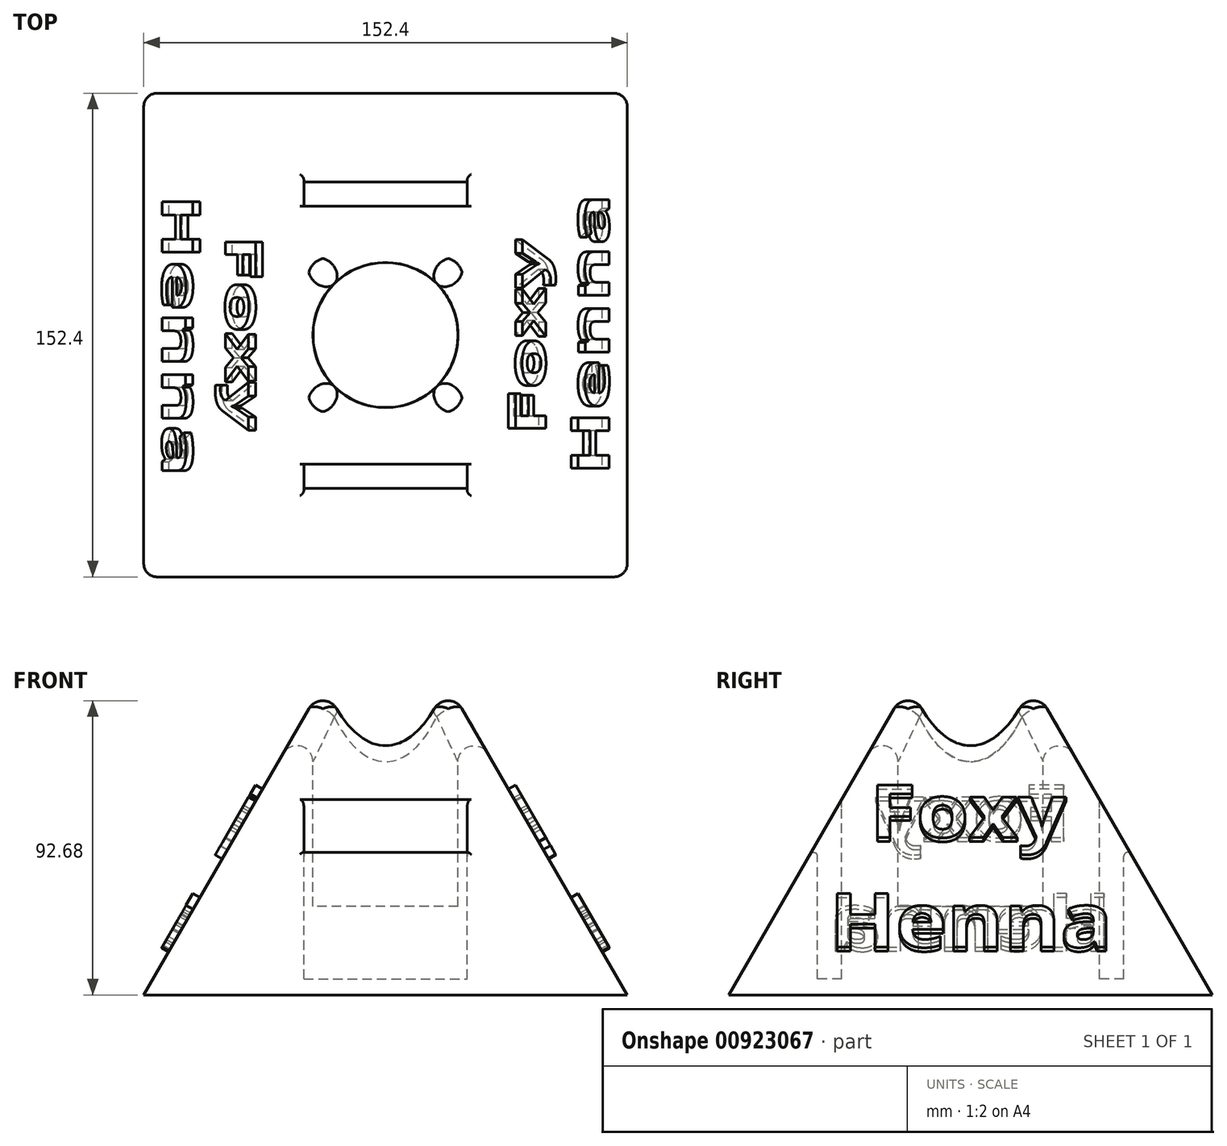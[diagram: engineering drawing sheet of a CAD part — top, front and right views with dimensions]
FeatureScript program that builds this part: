
annotation { "Feature Type Name" : "Feature", "Feature Type Description" : "" }
export const myFeature = defineFeature(function(context is Context, id is Id, definition is map)
    precondition{}
    {
        {
            var Q0;
            Q0=qCreatedBy(makeId("Front.planeOp"),FACE);
            var sketch = newSketch(context, id + "F0", { "sketchPlane" : qUnion([Q0])});
            skLineSegment(sketch, "E0.bottom", {"start": v(-76.2, 65.99) * mm, "end": v(76.2, 65.99) * mm});
            skLineSegment(sketch, "E0.top", {"start": v(-76.2, -65.99) * mm, "end": v(76.2, -65.99) * mm});
            skLineSegment(sketch, "E0.left", {"start": v(-76.2, 65.99) * mm, "end": v(-76.2, -65.99) * mm});
            skLineSegment(sketch, "E0.right", {"start": v(76.2, 65.99) * mm, "end": v(76.2, -65.99) * mm});
            skSolve(sketch);
        }
        {
            var Q0;
            Q0 = qSketchRegion(id + "F0", true);
            extrude(context, id + "F1", {"entities" : qUnion([Q0]), "endBound" : BoundingType.SYMMETRIC, "depth" : 152.4 * mm, "offsetDistance" : 25.4 * mm});
        }
        {
            var Q0;
            Q0=makeQuery(id+"F1.opExtrude","CAP_FACE",FACE,{"disambiguationData":[OSD([sQuery(id+"F0.wireOp",EDGE,"E0.bottom"),sQuery(id+"F0.wireOp",EDGE,"E0.top"),sQuery(id+"F0.wireOp",EDGE,"E0.left"),sQuery(id+"F0.wireOp",EDGE,"E0.right")])],"isStart":false});
            var sketch = newSketch(context, id + "F2", { "sketchPlane" : qUnion([Q0])});
            skLineSegment(sketch, "E1", {"start": v(-76.2, -65.99) * mm, "end": v(0, 65.99) * mm});
            skLineSegment(sketch, "E2", {"start": v(0, 65.99) * mm, "end": v(76.2, -65.99) * mm});
            skLineSegment(sketch, "E3", {"start": v(-76.2, -65.99) * mm, "end": v(-84.92, -65.99) * mm});
            skLineSegment(sketch, "E4", {"start": v(-84.92, -65.99) * mm, "end": v(-84.92, 72.24) * mm});
            skLineSegment(sketch, "E5", {"start": v(-84.92, 72.24) * mm, "end": v(80.83, 72.24) * mm});
            skLineSegment(sketch, "E6", {"start": v(80.83, 72.24) * mm, "end": v(80.83, -65.99) * mm});
            skLineSegment(sketch, "E7", {"start": v(80.83, -65.99) * mm, "end": v(76.2, -65.99) * mm});
            skSolve(sketch);
        }
        {
            var Q0;
            Q0=makeQuery(id+"F1.opExtrude","SWEPT_FACE",FACE,{"disambiguationData":[OSD([sQuery(id+"F0.wireOp",EDGE,"E0.right")])]});
            var sketch = newSketch(context, id + "F3", { "sketchPlane" : qUnion([Q0])});
            skLineSegment(sketch, "E8", {"start": v(-76.2, -65.99) * mm, "end": v(0, 65.99) * mm});
            skLineSegment(sketch, "E9", {"start": v(0, 65.99) * mm, "end": v(76.2, -65.99) * mm});
            skLineSegment(sketch, "E10", {"start": v(76.2, -65.99) * mm, "end": v(99.8, -65.99) * mm});
            skLineSegment(sketch, "E11", {"start": v(99.8, -65.99) * mm, "end": v(99.8, 76.06) * mm});
            skLineSegment(sketch, "E12", {"start": v(99.8, 76.06) * mm, "end": v(-87, 76.06) * mm});
            skLineSegment(sketch, "E13", {"start": v(-87, 76.06) * mm, "end": v(-87, -65.99) * mm});
            skLineSegment(sketch, "E14", {"start": v(-87, -65.99) * mm, "end": v(-76.2, -65.99) * mm});
            skSolve(sketch);
        }
        {
            var Q0;
            Q0 = qSketchRegion(id + "F2", true);
            extrude(context, id + "F4", {"entities" : qUnion([Q0]), "operationType" : NewBodyOperationType.REMOVE, "oppositeDirection" : true, "depth" : 177.8 * mm, "offsetDistance" : 25.4 * mm});
        }
        {
            var Q0;
            Q0 = qSketchRegion(id + "F3", true);
            extrude(context, id + "F5", {"entities" : qUnion([Q0]), "operationType" : NewBodyOperationType.REMOVE, "oppositeDirection" : true, "depth" : 177.8 * mm, "offsetDistance" : 25.4 * mm});
        }
        {
            var Q0;
            Q0=qCreatedBy(makeId("Top.planeOp"),FACE);
            var sketch = newSketch(context, id + "F6", { "sketchPlane" : qUnion([Q0])});
            skCircle(sketch, "E15", {"center": v(0, 0) * mm, "radius": 22.86 * mm});
            skSolve(sketch);
        }
        {
            var Q0;
            Q0 = qSketchRegion(id + "F6", true);
            extrude(context, id + "F7", {"entities" : qUnion([Q0]), "operationType" : NewBodyOperationType.REMOVE, "oppositeDirection" : true, "depth" : 38.1 * mm, "offsetDistance" : 25.4 * mm});
        }
        {
            var Q0;
            Q0 = qSketchRegion(id + "F6", true);
            extrude(context, id + "F8", {"entities" : qUnion([Q0]), "operationType" : NewBodyOperationType.REMOVE, "depth" : 76.2 * mm, "offsetDistance" : 25.4 * mm});
        }
        {
            var Q0;
            Q0=qCreatedBy(makeId("Top.planeOp"),FACE);
            var sketch = newSketch(context, id + "F9", { "sketchPlane" : qUnion([Q0])});
            skLineSegment(sketch, "E16.bottom", {"start": v(-25.72, -40.64) * mm, "end": v(25.72, -40.64) * mm});
            skLineSegment(sketch, "E16.top", {"start": v(-25.72, -48.26) * mm, "end": v(25.72, -48.26) * mm});
            skLineSegment(sketch, "E16.left", {"start": v(-25.72, -40.64) * mm, "end": v(-25.72, -48.26) * mm});
            skLineSegment(sketch, "E16.right", {"start": v(25.72, -40.64) * mm, "end": v(25.72, -48.26) * mm});
            skLineSegment(sketch, "E17.bottom", {"start": v(-25.72, 48.26) * mm, "end": v(25.72, 48.26) * mm});
            skLineSegment(sketch, "E17.top", {"start": v(-25.72, 40.64) * mm, "end": v(25.72, 40.64) * mm});
            skLineSegment(sketch, "E17.left", {"start": v(-25.72, 48.26) * mm, "end": v(-25.72, 40.64) * mm});
            skLineSegment(sketch, "E17.right", {"start": v(25.72, 48.26) * mm, "end": v(25.72, 40.64) * mm});
            skSolve(sketch);
        }
        {
            var Q0;
            Q0 = qSketchRegion(id + "F9", true);
            extrude(context, id + "F10", {"entities" : qUnion([Q0]), "operationType" : NewBodyOperationType.REMOVE, "oppositeDirection" : true, "depth" : 60.96 * mm, "offsetDistance" : 25.4 * mm});
        }
        {
            var Q0;
            Q0=makeQuery(id+"F8.boolean.opBoolean","INTERSECT",EDGE,{"derivedFrom":[makeQuery(id+"F5.boolean.opBoolean","COPY",FACE,{"derivedFrom":makeQuery(id+"F5.opExtrude","SWEPT_FACE",FACE,{"disambiguationData":[OSD([sQuery(id+"F3.wireOp",EDGE,"E8")])]})}),makeQuery(id+"F8.opExtrude","SWEPT_FACE",FACE,{"disambiguationData":[OSD([sQuery(id+"F6.wireOp",EDGE,"E15")])]})]});
            var Q1;
            Q1=makeQuery(id+"F8.boolean.opBoolean","INTERSECT",EDGE,{"derivedFrom":[makeQuery(id+"F4.boolean.opBoolean","COPY",FACE,{"derivedFrom":makeQuery(id+"F4.opExtrude","SWEPT_FACE",FACE,{"disambiguationData":[OSD([sQuery(id+"F2.wireOp",EDGE,"E2")])]})}),makeQuery(id+"F8.opExtrude","SWEPT_FACE",FACE,{"disambiguationData":[OSD([sQuery(id+"F6.wireOp",EDGE,"E15")])]})]});
            var Q2;
            Q2=makeQuery(id+"F8.boolean.opBoolean","INTERSECT",EDGE,{"derivedFrom":[makeQuery(id+"F5.boolean.opBoolean","COPY",FACE,{"derivedFrom":makeQuery(id+"F5.opExtrude","SWEPT_FACE",FACE,{"disambiguationData":[OSD([sQuery(id+"F3.wireOp",EDGE,"E9")])]})}),makeQuery(id+"F8.opExtrude","SWEPT_FACE",FACE,{"disambiguationData":[OSD([sQuery(id+"F6.wireOp",EDGE,"E15")])]})]});
            var Q3;
            Q3=makeQuery(id+"F8.boolean.opBoolean","INTERSECT",EDGE,{"derivedFrom":[makeQuery(id+"F4.boolean.opBoolean","COPY",FACE,{"derivedFrom":makeQuery(id+"F4.opExtrude","SWEPT_FACE",FACE,{"disambiguationData":[OSD([sQuery(id+"F2.wireOp",EDGE,"E1")])]})}),makeQuery(id+"F8.opExtrude","SWEPT_FACE",FACE,{"disambiguationData":[OSD([sQuery(id+"F6.wireOp",EDGE,"E15")])]})]});
            fillet(context, id + "F11", {"entities" : qUnion([Q0, Q1, Q2, Q3]), "radius" : 5.08 * mm, "tangentPropagation" : true, "allowEdgeOverflow" : false});
        }
        {
            var Q0;
            {var subQ0=makeQuery(id+"F8.opExtrude","SWEPT_FACE",FACE,{"disambiguationData":[OSD([sQuery(id+"F6.wireOp",EDGE,"E15")])]});Q0=makeQuery(id+"F11.opFillet","BLEND_EDGE",EDGE,{"blendedFrom":[makeQuery(id+"F8.boolean.opBoolean","INTERSECT",EDGE,{"derivedFrom":[makeQuery(id+"F5.boolean.opBoolean","COPY",FACE,{"derivedFrom":makeQuery(id+"F5.opExtrude","SWEPT_FACE",FACE,{"disambiguationData":[OSD([sQuery(id+"F3.wireOp",EDGE,"E8")])]})}),subQ0]}),makeQuery(id+"F8.boolean.opBoolean","INTERSECT",EDGE,{"derivedFrom":[makeQuery(id+"F4.boolean.opBoolean","COPY",FACE,{"derivedFrom":makeQuery(id+"F4.opExtrude","SWEPT_FACE",FACE,{"disambiguationData":[OSD([sQuery(id+"F2.wireOp",EDGE,"E1")])]})}),subQ0]})],"blendedInto":[]});}
            var Q1;
            {var subQ0=makeQuery(id+"F8.opExtrude","SWEPT_FACE",FACE,{"disambiguationData":[OSD([sQuery(id+"F6.wireOp",EDGE,"E15")])]});Q1=makeQuery(id+"F11.opFillet","BLEND_EDGE",EDGE,{"blendedFrom":[makeQuery(id+"F8.boolean.opBoolean","INTERSECT",EDGE,{"derivedFrom":[makeQuery(id+"F5.boolean.opBoolean","COPY",FACE,{"derivedFrom":makeQuery(id+"F5.opExtrude","SWEPT_FACE",FACE,{"disambiguationData":[OSD([sQuery(id+"F3.wireOp",EDGE,"E9")])]})}),subQ0]}),makeQuery(id+"F8.boolean.opBoolean","INTERSECT",EDGE,{"derivedFrom":[makeQuery(id+"F4.boolean.opBoolean","COPY",FACE,{"derivedFrom":makeQuery(id+"F4.opExtrude","SWEPT_FACE",FACE,{"disambiguationData":[OSD([sQuery(id+"F2.wireOp",EDGE,"E1")])]})}),subQ0]})],"blendedInto":[]});}
            var Q2;
            {var subQ0=makeQuery(id+"F8.opExtrude","SWEPT_FACE",FACE,{"disambiguationData":[OSD([sQuery(id+"F6.wireOp",EDGE,"E15")])]});Q2=makeQuery(id+"F11.opFillet","BLEND_EDGE",EDGE,{"blendedFrom":[makeQuery(id+"F8.boolean.opBoolean","INTERSECT",EDGE,{"derivedFrom":[makeQuery(id+"F5.boolean.opBoolean","COPY",FACE,{"derivedFrom":makeQuery(id+"F5.opExtrude","SWEPT_FACE",FACE,{"disambiguationData":[OSD([sQuery(id+"F3.wireOp",EDGE,"E9")])]})}),subQ0]}),makeQuery(id+"F8.boolean.opBoolean","INTERSECT",EDGE,{"derivedFrom":[makeQuery(id+"F4.boolean.opBoolean","COPY",FACE,{"derivedFrom":makeQuery(id+"F4.opExtrude","SWEPT_FACE",FACE,{"disambiguationData":[OSD([sQuery(id+"F2.wireOp",EDGE,"E2")])]})}),subQ0]})],"blendedInto":[]});}
            var Q3;
            {var subQ0=makeQuery(id+"F8.opExtrude","SWEPT_FACE",FACE,{"disambiguationData":[OSD([sQuery(id+"F6.wireOp",EDGE,"E15")])]});Q3=makeQuery(id+"F11.opFillet","BLEND_EDGE",EDGE,{"blendedFrom":[makeQuery(id+"F8.boolean.opBoolean","INTERSECT",EDGE,{"derivedFrom":[makeQuery(id+"F5.boolean.opBoolean","COPY",FACE,{"derivedFrom":makeQuery(id+"F5.opExtrude","SWEPT_FACE",FACE,{"disambiguationData":[OSD([sQuery(id+"F3.wireOp",EDGE,"E8")])]})}),subQ0]}),makeQuery(id+"F8.boolean.opBoolean","INTERSECT",EDGE,{"derivedFrom":[makeQuery(id+"F4.boolean.opBoolean","COPY",FACE,{"derivedFrom":makeQuery(id+"F4.opExtrude","SWEPT_FACE",FACE,{"disambiguationData":[OSD([sQuery(id+"F2.wireOp",EDGE,"E2")])]})}),subQ0]})],"blendedInto":[]});}
            fillet(context, id + "F12", {"entities" : qUnion([Q0, Q1, Q2, Q3]), "radius" : 5.08 * mm, "tangentPropagation" : true, "allowEdgeOverflow" : false});
        }
        {
            var Q0;
            Q0=makeQuery(id+"F4.boolean.opBoolean","COPY",FACE,{"derivedFrom":makeQuery(id+"F4.opExtrude","SWEPT_FACE",FACE,{"disambiguationData":[OSD([sQuery(id+"F2.wireOp",EDGE,"E2")])]})});
            var sketch = newSketch(context, id + "F13", { "sketchPlane" : qUnion([Q0])});
            skText(sketch, "E18", { "text": "Foxy", "fontName": "OpenSans-Bold.ttf"});
            skText(sketch, "E19", { "text": "Henna", "fontName": "OpenSans-Bold.ttf"});
            const initialGuessF13  = {"E18": [-0.03175, -0.03937, 1, 0, 0.01921], "E19": [-0.04445, -0.0793, 1, 0, 0.01961]};
            skSetInitialGuess(sketch, initialGuessF13);
            skSolve(sketch);
        }
        {
            var Q0;
            Q0 = qSketchRegion(id + "F13", true);
            extrude(context, id + "F14", {"entities" : qUnion([Q0]), "operationType" : NewBodyOperationType.ADD, "depth" : 2.54 * mm, "offsetDistance" : 25.4 * mm});
        }
        {
            var Q0;
            Q0=makeQuery(id+"F4.boolean.opBoolean","COPY",FACE,{"derivedFrom":makeQuery(id+"F4.opExtrude","SWEPT_FACE",FACE,{"disambiguationData":[OSD([sQuery(id+"F2.wireOp",EDGE,"E1")])]})});
            var sketch = newSketch(context, id + "F15", { "sketchPlane" : qUnion([Q0])});
            skText(sketch, "E20", { "text": "Foxy", "fontName": "OpenSans-Bold.ttf"});
            skText(sketch, "E21", { "text": "Henna", "fontName": "OpenSans-Bold.ttf"});
            const initialGuessF15  = {"E20": [-0.03175, -0.03937, 1, 0, 0.01921], "E21": [-0.04445, -0.0793, 1, 0, 0.01961]};
            skSetInitialGuess(sketch, initialGuessF15);
            skSolve(sketch);
        }
        {
            var Q0;
            Q0 = qSketchRegion(id + "F15", true);
            extrude(context, id + "F16", {"entities" : qUnion([Q0]), "operationType" : NewBodyOperationType.ADD, "depth" : 2.54 * mm, "offsetDistance" : 25.4 * mm});
        }
        {
            var Q0;
            Q0=makeQuery(id+"F10.boolean.opBoolean","INTERSECT",EDGE,{"derivedFrom":[makeQuery(id+"F5.boolean.opBoolean","COPY",FACE,{"derivedFrom":makeQuery(id+"F5.opExtrude","SWEPT_FACE",FACE,{"disambiguationData":[OSD([sQuery(id+"F3.wireOp",EDGE,"E9")])]})}),makeQuery(id+"F10.opExtrude","SWEPT_FACE",FACE,{"disambiguationData":[OSD([sQuery(id+"F9.wireOp",EDGE,"E17.left")])]})]});
            var Q1;
            Q1=makeQuery(id+"F10.boolean.opBoolean","INTERSECT",EDGE,{"derivedFrom":[makeQuery(id+"F5.boolean.opBoolean","COPY",FACE,{"derivedFrom":makeQuery(id+"F5.opExtrude","SWEPT_FACE",FACE,{"disambiguationData":[OSD([sQuery(id+"F3.wireOp",EDGE,"E9")])]})}),makeQuery(id+"F10.opExtrude","SWEPT_FACE",FACE,{"disambiguationData":[OSD([sQuery(id+"F9.wireOp",EDGE,"E17.right")])]})]});
            var Q2;
            Q2=makeQuery(id+"F10.boolean.opBoolean","INTERSECT",EDGE,{"derivedFrom":[makeQuery(id+"F5.boolean.opBoolean","COPY",FACE,{"derivedFrom":makeQuery(id+"F5.opExtrude","SWEPT_FACE",FACE,{"disambiguationData":[OSD([sQuery(id+"F3.wireOp",EDGE,"E8")])]})}),makeQuery(id+"F10.opExtrude","SWEPT_FACE",FACE,{"disambiguationData":[OSD([sQuery(id+"F9.wireOp",EDGE,"E16.right")])]})]});
            var Q3;
            Q3=makeQuery(id+"F10.boolean.opBoolean","INTERSECT",EDGE,{"derivedFrom":[makeQuery(id+"F5.boolean.opBoolean","COPY",FACE,{"derivedFrom":makeQuery(id+"F5.opExtrude","SWEPT_FACE",FACE,{"disambiguationData":[OSD([sQuery(id+"F3.wireOp",EDGE,"E8")])]})}),makeQuery(id+"F10.opExtrude","SWEPT_FACE",FACE,{"disambiguationData":[OSD([sQuery(id+"F9.wireOp",EDGE,"E16.left")])]})]});
            fillet(context, id + "F17", {"entities" : qUnion([Q0, Q1, Q2, Q3]), "radius" : 1.27 * mm, "tangentPropagation" : true, "allowEdgeOverflow" : false});
        }
        {
            var Q0;
            Q0=makeQuery(id+"F10.boolean.opBoolean","INTERSECT",EDGE,{"derivedFrom":[makeQuery(id+"F5.boolean.opBoolean","COPY",FACE,{"derivedFrom":makeQuery(id+"F5.opExtrude","SWEPT_FACE",FACE,{"disambiguationData":[OSD([sQuery(id+"F3.wireOp",EDGE,"E9")])]})}),makeQuery(id+"F10.opExtrude","SWEPT_FACE",FACE,{"disambiguationData":[OSD([sQuery(id+"F9.wireOp",EDGE,"E17.bottom")])]})]});
            var Q1;
            Q1=makeQuery(id+"F10.boolean.opBoolean","INTERSECT",EDGE,{"derivedFrom":[makeQuery(id+"F5.boolean.opBoolean","COPY",FACE,{"derivedFrom":makeQuery(id+"F5.opExtrude","SWEPT_FACE",FACE,{"disambiguationData":[OSD([sQuery(id+"F3.wireOp",EDGE,"E8")])]})}),makeQuery(id+"F10.opExtrude","SWEPT_FACE",FACE,{"disambiguationData":[OSD([sQuery(id+"F9.wireOp",EDGE,"E16.top")])]})]});
            fillet(context, id + "F18", {"entities" : qUnion([Q0, Q1]), "radius" : 1.27 * mm, "tangentPropagation" : true, "allowEdgeOverflow" : false});
        }
    });
